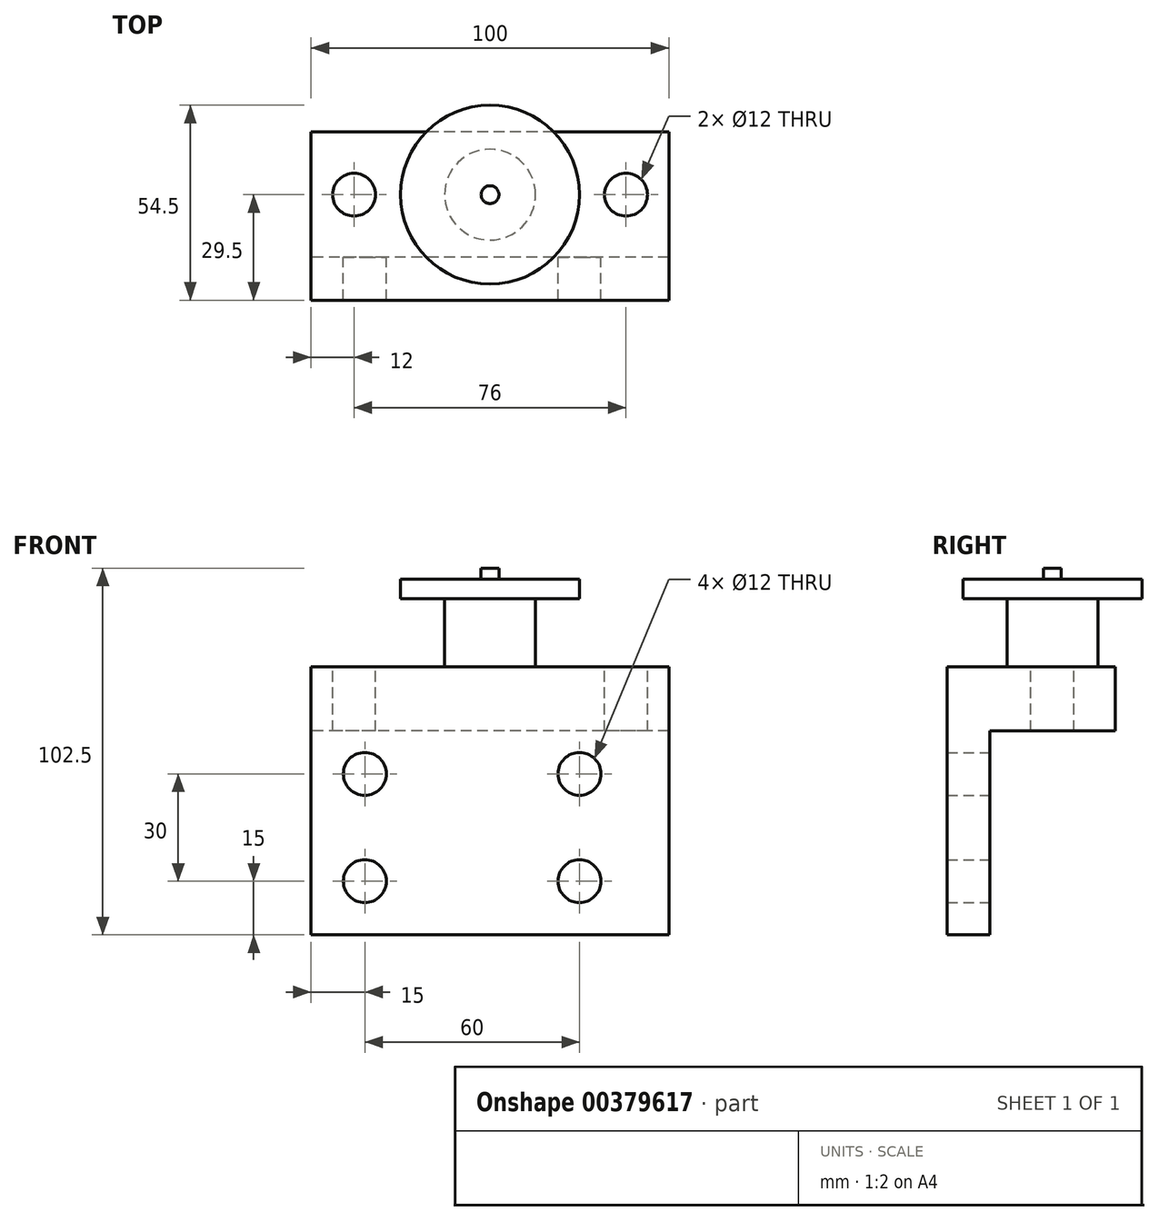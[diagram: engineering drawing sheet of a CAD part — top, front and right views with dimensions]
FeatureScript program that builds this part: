
annotation { "Feature Type Name" : "Feature", "Feature Type Description" : "" }
export const myFeature = defineFeature(function(context is Context, id is Id, definition is map)
    precondition{}
    {
        {
            var Q0;
            Q0=qCreatedBy(makeId("Top.planeOp"),FACE);
            var sketch = newSketch(context, id + "F0", { "sketchPlane" : qUnion([Q0])});
            skLineSegment(sketch, "E0.bottom", {"start": v(50, -17.5) * mm, "end": v(-50, -17.5) * mm});
            skLineSegment(sketch, "E0.top", {"start": v(50, 17.5) * mm, "end": v(-50, 17.5) * mm});
            skLineSegment(sketch, "E0.left", {"start": v(50, -17.5) * mm, "end": v(50, 17.5) * mm});
            skLineSegment(sketch, "E0.right", {"start": v(-50, -17.5) * mm, "end": v(-50, 17.5) * mm});
            skPoint(sketch, "E0.middle", {"position": v(0, 0) * mm});
            skSolve(sketch);
        }
        {
            var Q0;
            Q0=makeQuery(id+"F0.imprint","IMPRINT",FACE,{"disambiguationData":[TD([[makeQuery(id+"F0.imprint","IMPRINT",EDGE,{"derivedFrom":sQuery(id+"F0.wireOp",EDGE,"E0.bottom")}),-1.0]])]});
            extrude(context, id + "F1", {"entities" : qUnion([Q0]), "depth" : -18 * mm});
        }
        {
            var Q0;
            Q0=makeQuery(id+"F1.opExtrude","CAP_FACE",FACE,{"disambiguationData":[OSD([sQuery(id+"F0.wireOp",EDGE,"E0.bottom"),sQuery(id+"F0.wireOp",EDGE,"E0.top"),sQuery(id+"F0.wireOp",EDGE,"E0.left"),sQuery(id+"F0.wireOp",EDGE,"E0.right")])],"isStart":true});
            var sketch = newSketch(context, id + "F2", { "sketchPlane" : qUnion([Q0])});
            skLineSegment(sketch, "E1", {"start": v(50, 0) * mm, "end": v(38, 0) * mm, "construction": true});
            skLineSegment(sketch, "E2", {"start": v(-50, 0) * mm, "end": v(-38, 0) * mm, "construction": true});
            skCircle(sketch, "E3", {"center": v(38, 0) * mm, "radius": 6 * mm});
            skCircle(sketch, "E4", {"center": v(-38, 0) * mm, "radius": 6 * mm});
            skSolve(sketch);
        }
        {
            var Q0;
            Q0=sQuery(id+"F2.wireOp",VERTEX,"E2.end");
            var Q1;
            Q1=sQuery(id+"F2.wireOp",VERTEX,"E3.center");
            var Q2;
            Q2=makeQuery(id+"F1.opExtrude","SWEPT_BODY",BODY,{"disambiguationData":[OSD([sQuery(id+"F0.wireOp",EDGE,"E0.bottom"),sQuery(id+"F0.wireOp",EDGE,"E0.top"),sQuery(id+"F0.wireOp",EDGE,"E0.left"),sQuery(id+"F0.wireOp",EDGE,"E0.right")])]});
            hole(context, id + "F3", {"style" : HoleStyle.SIMPLE, "endStyle" : HoleEndStyle.THROUGH, "holeDiameter" : 12 * mm, "isTappedThrough" : true, "tappedDepth" : 12 * mm, "tapClearance" : 3, "locations" : qUnion([Q0, Q1]), "scope" : qUnion([Q2])});
        }
        {
            var Q0;
            Q0=makeQuery(id+"F1.opExtrude","CAP_FACE",FACE,{"disambiguationData":[OSD([sQuery(id+"F0.wireOp",EDGE,"E0.bottom"),sQuery(id+"F0.wireOp",EDGE,"E0.top"),sQuery(id+"F0.wireOp",EDGE,"E0.left"),sQuery(id+"F0.wireOp",EDGE,"E0.right")])],"isStart":true});
            var sketch = newSketch(context, id + "F4", { "sketchPlane" : qUnion([Q0])});
            skCircle(sketch, "E5", {"center": v(0, 0) * mm, "radius": 12.7 * mm});
            skSolve(sketch);
        }
        {
            var Q0;
            Q0=makeQuery(id+"F4.imprint","IMPRINT",FACE,{"disambiguationData":[TD([[makeQuery(id+"F4.imprint","IMPRINT",EDGE,{"derivedFrom":sQuery(id+"F4.wireOp",EDGE,"E5")}),1.0]])]});
            extrude(context, id + "F5", {"entities" : qUnion([Q0]), "operationType" : NewBodyOperationType.ADD, "depth" : 19 * mm});
        }
        {
            var Q0;
            Q0=makeQuery(id+"F5.opExtrude","CAP_FACE",FACE,{"disambiguationData":[OSD([sQuery(id+"F4.wireOp",EDGE,"E5")])],"isStart":false});
            var sketch = newSketch(context, id + "F6", { "sketchPlane" : qUnion([Q0])});
            skCircle(sketch, "E6", {"center": v(0, 0) * mm, "radius": 25 * mm});
            skSolve(sketch);
        }
        {
            var Q0;
            Q0=makeQuery(id+"F6.imprint","IMPRINT",FACE,{"disambiguationData":[TD([[makeQuery(id+"F6.imprint","IMPRINT",EDGE,{"derivedFrom":sQuery(id+"F6.wireOp",EDGE,"E6")}),1.0]])]});
            var Q1;
            Q1=makeQuery(id+"F6.imprint","IMPRINT",FACE,{"disambiguationData":[TD([[makeQuery(id+"F6.imprint","IMPRINT",EDGE,{"derivedFrom":makeQuery(id+"F5.opExtrude","CAP_EDGE",EDGE,{"disambiguationData":[OSD([sQuery(id+"F4.wireOp",EDGE,"E5")])],"isStart":false})}),1.0]])]});
            extrude(context, id + "F7", {"entities" : qUnion([Q0, Q1]), "operationType" : NewBodyOperationType.ADD, "depth" : 5.5 * mm});
        }
        {
            var Q0;
            Q0=makeQuery(id+"F7.opExtrude","CAP_FACE",FACE,{"disambiguationData":[OSD([sQuery(id+"F6.wireOp",EDGE,"E6")])],"isStart":false});
            var sketch = newSketch(context, id + "F8", { "sketchPlane" : qUnion([Q0])});
            skCircle(sketch, "E7", {"center": v(0, 0) * mm, "radius": 2.5 * mm});
            skSolve(sketch);
        }
        {
            var Q0;
            Q0=qSketchRegion(id+"F8",true);
            extrude(context, id + "F9", {"entities" : qUnion([Q0]), "operationType" : NewBodyOperationType.ADD, "depth" : 3 * mm});
        }
        {
            var Q0;
            Q0=makeQuery(id+"F1.opExtrude","SWEPT_FACE",FACE,{"disambiguationData":[OSD([sQuery(id+"F0.wireOp",EDGE,"E0.bottom")])]});
            var sketch = newSketch(context, id + "F10", { "sketchPlane" : qUnion([Q0])});
            skLineSegment(sketch, "E8.bottom", {"start": v(-50, 0) * mm, "end": v(50, 0) * mm});
            skLineSegment(sketch, "E8.top", {"start": v(-50, -75) * mm, "end": v(50, -75) * mm});
            skLineSegment(sketch, "E8.left", {"start": v(-50, 0) * mm, "end": v(-50, -75) * mm});
            skLineSegment(sketch, "E8.right", {"start": v(50, 0) * mm, "end": v(50, -75) * mm});
            skSolve(sketch);
        }
        {
            var Q0;
            {var subQ0=sQuery(id+"F10.wireOp",EDGE,"E8.top");Q0=makeQuery(id+"F10.imprint","IMPRINT",FACE,{"disambiguationData":[TD([[makeQuery(id+"F10.imprint","IMPRINT",EDGE,{"derivedFrom":subQ0}),1.0]])]});}
            var Q1;
            {var subQ0=sQuery(id+"F10.wireOp",EDGE,"E8.bottom");Q1=makeQuery(id+"F10.imprint","IMPRINT",FACE,{"disambiguationData":[TD([[makeQuery(id+"F10.imprint","IMPRINT",EDGE,{"derivedFrom":subQ0}),1.0]])]});}
            extrude(context, id + "F11", {"entities" : qUnion([Q0, Q1]), "operationType" : NewBodyOperationType.ADD, "depth" : 12 * mm});
        }
        {
            var Q0;
            Q0=makeQuery(id+"F11.opExtrude","CAP_FACE",FACE,{"disambiguationData":[OSD([sQuery(id+"F10.wireOp",EDGE,"E8.bottom"),sQuery(id+"F10.wireOp",EDGE,"E8.top"),sQuery(id+"F10.wireOp",EDGE,"E8.left"),sQuery(id+"F10.wireOp",EDGE,"E8.right")])],"isStart":true});
            var sketch = newSketch(context, id + "F12", { "sketchPlane" : qUnion([Q0])});
            skLineSegment(sketch, "E9", {"start": v(50, -75) * mm, "end": v(50, -60) * mm, "construction": true});
            skLineSegment(sketch, "E10", {"start": v(50, -18) * mm, "end": v(50, -30) * mm, "construction": true});
            skLineSegment(sketch, "E11", {"start": v(50, -30) * mm, "end": v(35, -30) * mm, "construction": true});
            skLineSegment(sketch, "E12", {"start": v(35, -30) * mm, "end": v(-25, -30) * mm, "construction": true});
            skLineSegment(sketch, "E13", {"start": v(50, -60) * mm, "end": v(35, -60) * mm, "construction": true});
            skLineSegment(sketch, "E14", {"start": v(35, -60) * mm, "end": v(-25, -60) * mm, "construction": true});
            skLineSegment(sketch, "E15", {"start": v(50, -60) * mm, "end": v(50, -30) * mm, "construction": true});
            skSolve(sketch);
        }
        {
            var Q0;
            Q0=sQuery(id+"F12.wireOp",VERTEX,"E12.end");
            var Q1;
            Q1=sQuery(id+"F12.wireOp",VERTEX,"E14.end");
            var Q2;
            Q2=sQuery(id+"F12.wireOp",VERTEX,"E14.start");
            var Q3;
            Q3=sQuery(id+"F12.wireOp",VERTEX,"E12.start");
            var Q4;
            Q4=makeQuery(id+"F1.opExtrude","SWEPT_BODY",BODY,{"disambiguationData":[OSD([sQuery(id+"F0.wireOp",EDGE,"E0.bottom"),sQuery(id+"F0.wireOp",EDGE,"E0.top"),sQuery(id+"F0.wireOp",EDGE,"E0.left"),sQuery(id+"F0.wireOp",EDGE,"E0.right")])]});
            hole(context, id + "F13", {"style" : HoleStyle.SIMPLE, "endStyle" : HoleEndStyle.THROUGH, "holeDiameter" : 12 * mm, "isTappedThrough" : true, "tappedDepth" : 12 * mm, "tapClearance" : 3, "locations" : qUnion([Q0, Q1, Q2, Q3]), "scope" : qUnion([Q4])});
        }
    });
